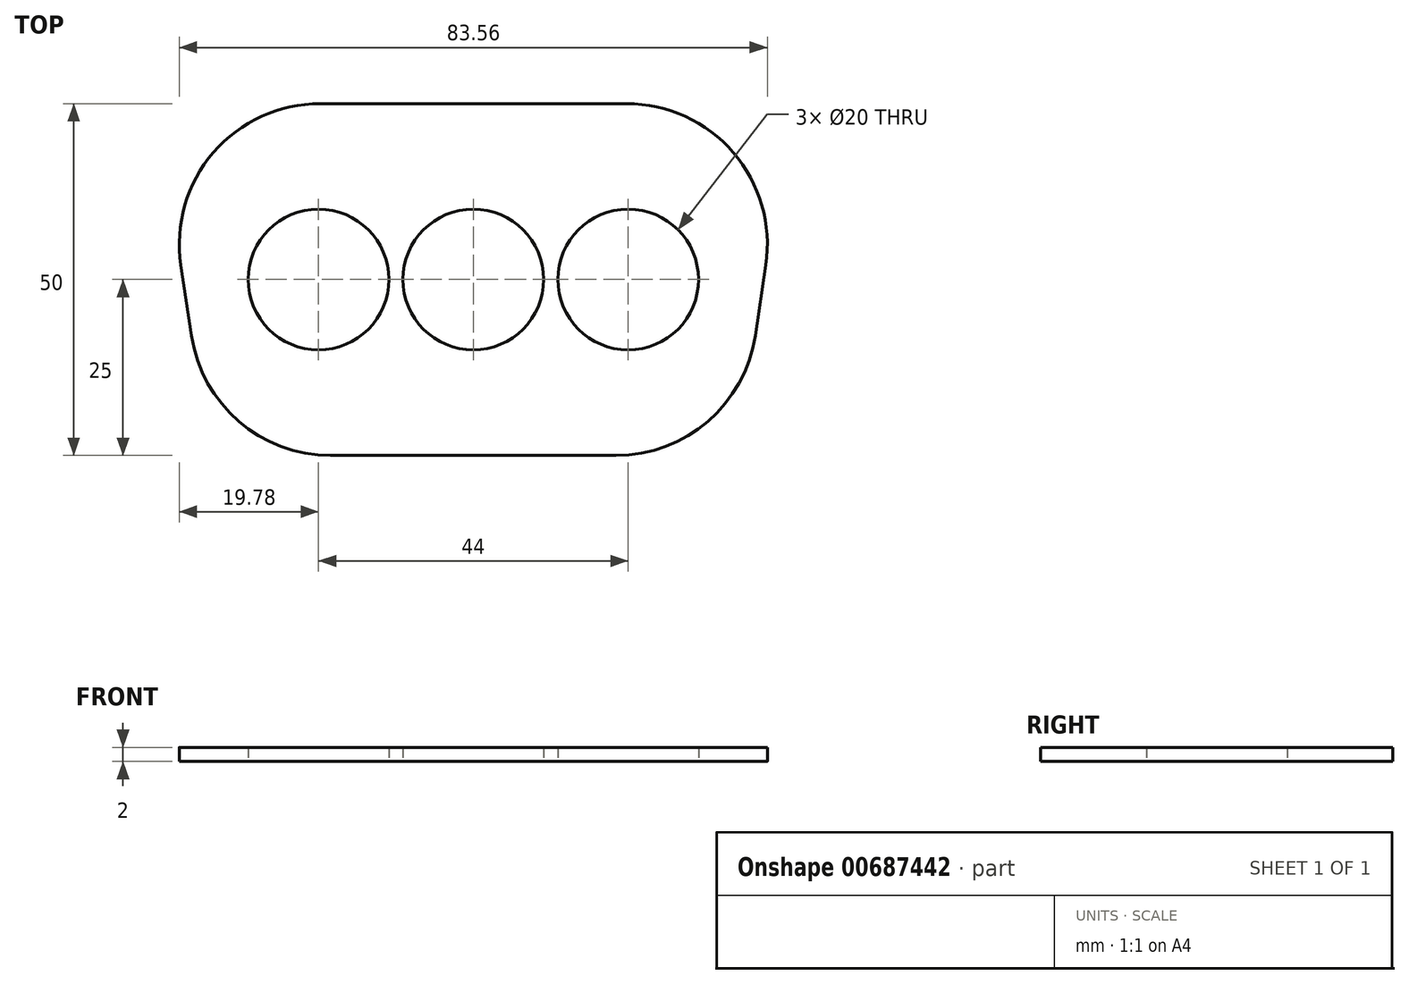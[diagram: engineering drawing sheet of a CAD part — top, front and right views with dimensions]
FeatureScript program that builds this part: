
annotation { "Feature Type Name" : "Feature", "Feature Type Description" : "" }
export const myFeature = defineFeature(function(context is Context, id is Id, definition is map)
    precondition{}
    {
        {
            var Q0;
            Q0=qCreatedBy(makeId("Top.planeOp"),FACE);
            var sketch = newSketch(context, id + "F0", { "sketchPlane" : qUnion([Q0])});
            skLineSegment(sketch, "E0", {"start": v(-45, 0) * mm, "end": v(45, 0) * mm});
            skLineSegment(sketch, "E1", {"start": v(-37.5, -50) * mm, "end": v(37.5, -50) * mm});
            skLineSegment(sketch, "E2", {"start": v(0, 0) * mm, "end": v(0, -50) * mm});
            skLineSegment(sketch, "E3", {"start": v(-45, 0) * mm, "end": v(-37.5, -50) * mm});
            skLineSegment(sketch, "E4", {"start": v(37.5, -50) * mm, "end": v(45, 0) * mm});
            skCircle(sketch, "E5", {"center": v(0, -25) * mm, "radius": 10 * mm});
            skCircle(sketch, "E6", {"center": v(-22, -25) * mm, "radius": 10 * mm});
            skCircle(sketch, "E7.MirrorC", {"center": v(22, -25) * mm, "radius": 10 * mm});
            skSolve(sketch);
        }
        {
            var Q0;
            Q0=qSketchRegion(id+"F0",true);
            extrude(context, id + "F1", {"entities" : qUnion([Q0]), "depth" : 2 * mm, "offsetDistance" : 25 * mm});
        }
        {
            var Q0;
            Q0=makeQuery(id+"F1.opExtrude","SWEPT_EDGE",EDGE,{"disambiguationData":[OSD([sQuery(id+"F0.wireOp",EDGE,"E1"),sQuery(id+"F0.wireOp",EDGE,"E3")])]});
            var Q1;
            Q1=makeQuery(id+"F1.opExtrude","SWEPT_EDGE",EDGE,{"disambiguationData":[OSD([sQuery(id+"F0.wireOp",EDGE,"E1"),sQuery(id+"F0.wireOp",EDGE,"E4")])]});
            var Q2;
            Q2=makeQuery(id+"F1.opExtrude","SWEPT_EDGE",EDGE,{"disambiguationData":[OSD([sQuery(id+"F0.wireOp",EDGE,"E0"),sQuery(id+"F0.wireOp",EDGE,"E4")])]});
            var Q3;
            Q3=makeQuery(id+"F1.opExtrude","SWEPT_EDGE",EDGE,{"disambiguationData":[OSD([sQuery(id+"F0.wireOp",EDGE,"E0"),sQuery(id+"F0.wireOp",EDGE,"E3")])]});
            fillet(context, id + "F2", {"entities" : qUnion([Q0, Q1, Q2, Q3]), "radius" : 20 * mm, "tangentPropagation" : true, "allowEdgeOverflow" : false});
        }
    });
